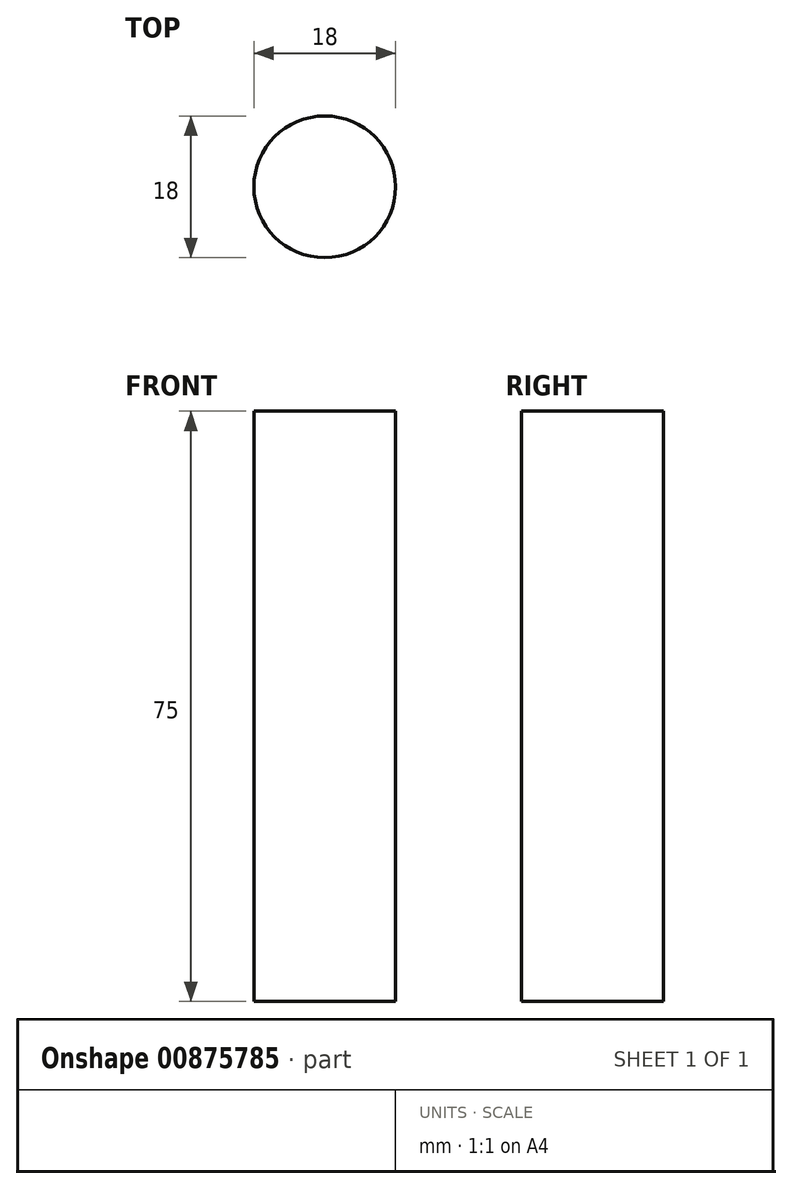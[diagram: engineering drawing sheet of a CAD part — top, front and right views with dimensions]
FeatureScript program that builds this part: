
annotation { "Feature Type Name" : "Feature", "Feature Type Description" : "" }
export const myFeature = defineFeature(function(context is Context, id is Id, definition is map)
    precondition{}
    {
        {
            var Q0;
            Q0=qCreatedBy(makeId("Top.planeOp"),FACE);
            var sketch = newSketch(context, id + "F0", { "sketchPlane" : qUnion([Q0])});
            skCircle(sketch, "E0", {"center": v(0, 0) * mm, "radius": 9 * mm});
            skSolve(sketch);
        }
        {
            var Q0;
            Q0 = qSketchRegion(id + "F0", true);
            extrude(context, id + "F1", {"entities" : qUnion([Q0]), "depth" : 75 * mm, "offsetDistance" : 25 * mm});
        }
    });
